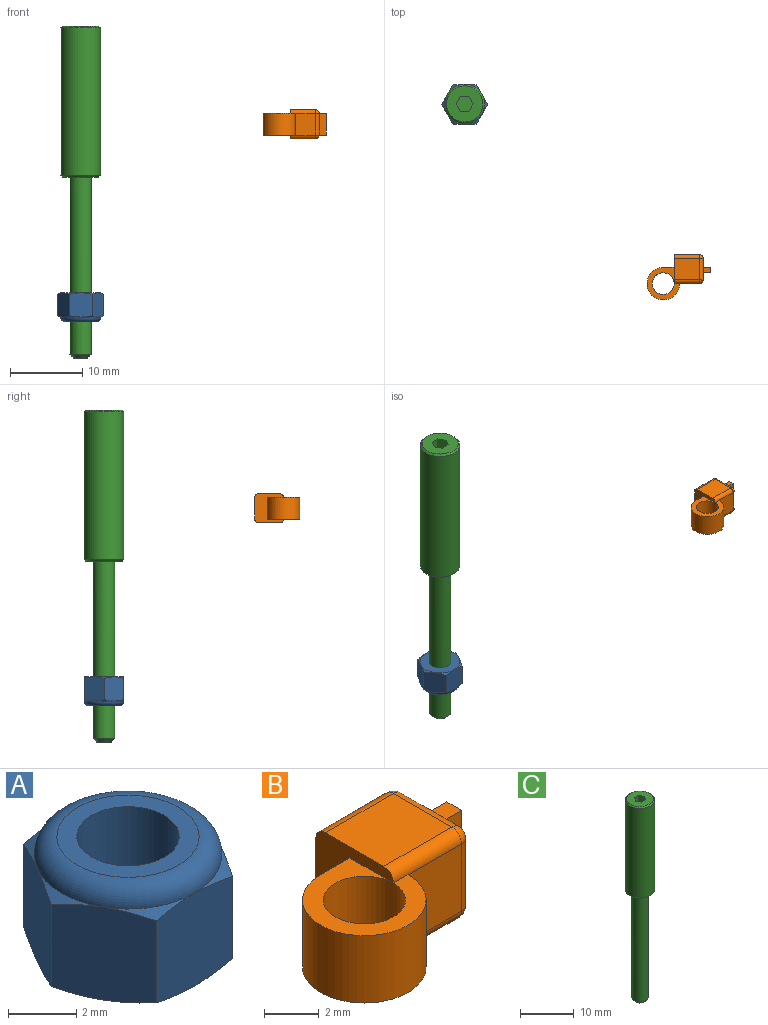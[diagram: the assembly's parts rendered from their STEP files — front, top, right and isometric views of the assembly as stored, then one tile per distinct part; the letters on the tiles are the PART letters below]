
ASSEMBLY  parts=3 mates=1
PART A: 22 faces, bbox 6.6x6.6x4.2 mm
  f0: plane 3.59x2.99mm, normal (-0.87,0.5,0), area 10.2mm2, adj f1,f5,f7,f9,f13,f14,f16,f21
  f1: plane 3.59x2.99mm, normal (-0.87,-0.5,0), area 10.2mm2, adj f0,f2,f7,f9,f10,f14,f20,f21
  f2: plane 3.6x3.42mm, normal (0,-1,0), area 10.2mm2, adj f1,f3,f7,f10,f11,f14,f19,f20
  f3: plane 3.59x2.99mm, normal (0.87,-0.5,0), area 10.2mm2, adj f2,f4,f7,f11,f12,f14,f18,f19
  f4: plane 3.59x2.99mm, normal (0.87,0.5,0), area 10.2mm2, adj f3,f5,f7,f12,f14,f15,f17,f18
  f5: plane 3.6x3.42mm, normal (0,1,0), area 10.2mm2, adj f0,f4,f7,f13,f14,f15,f16,f17
  f6: plane 4.17x4.17mm, normal (0,0,1), area 6.6mm2, adj f8,f14
  f7: plane 5.5x5.5mm, normal (0,0,-1), area 16.7mm2, adj f0,f1,f2,f3,f4,f5,f8,f16
  f8: cylinder r=1.5mm len=4mm, axis (0,0,1), area 37.7mm2, adj f6,f7
  f9: cone r=3.18mm half-angle=65deg, axis (0,0,-1), area 0.7mm2, adj f0,f1,f14
  f10: cone r=3.18mm half-angle=65deg, axis (0,0,-1), area 0.7mm2, adj f1,f2,f14
  f11: cone r=3.18mm half-angle=65deg, axis (0,0,-1), area 0.7mm2, adj f2,f3,f14
  f12: cone r=3.18mm half-angle=65deg, axis (0,0,-1), area 0.7mm2, adj f3,f4,f14
  f13: cone r=3.18mm half-angle=65deg, axis (0,0,-1), area 0.7mm2, adj f0,f5,f14
  f14: torus R=2.08mm, axis (0,0,-1), area 16.5mm2, adj f0,f1,f2,f3,f4,f5,f6,f9
  f15: cone r=3.18mm half-angle=65deg, axis (0,0,-1), area 0.7mm2, adj f4,f5,f14
  f16: cone r=2.75mm half-angle=65deg, axis (0,0,1), area 0.7mm2, adj f0,f5,f7
  f17: cone r=2.75mm half-angle=65deg, axis (0,0,1), area 0.7mm2, adj f4,f5,f7
  f18: cone r=2.75mm half-angle=65deg, axis (0,0,1), area 0.7mm2, adj f3,f4,f7
  f19: cone r=2.75mm half-angle=65deg, axis (0,0,1), area 0.7mm2, adj f2,f3,f7
  f20: cone r=2.75mm half-angle=65deg, axis (0,0,1), area 0.7mm2, adj f1,f2,f7
  f21: cone r=2.75mm half-angle=65deg, axis (0,0,1), area 0.7mm2, adj f0,f1,f7
PART B: 29 faces, bbox 8.8x6.3x4 mm
  f0: plane 3x1.25mm, normal (1,0,0), area 3.8mm2, adj f13,f18,f23,f24
  f1: cylinder r=2.25mm len=4.5mm, axis (0,0,-1), area 31.8mm2, adj f3,f4,f6,f16
  f2: cylinder r=1.5mm len=3mm, axis (0,0,-1), area 28.3mm2, adj f3,f4
  f3: plane 4.5x4.5mm, normal (0,0,1), area 8.2mm2, adj f1,f2,f5,f16,f22
  f4: plane 4.5x4.5mm, normal (0,0,-1), area 8.2mm2, adj f1,f2,f5,f16,f25
  f5: plane 4x4mm, normal (-1,0,0), area 9mm2, adj f3,f4,f8,f9,f10,f16,f17,f19
  f6: plane 3x2.75mm, normal (0,-1,0), area 8.2mm2, adj f1,f22,f25,f28
  f7: plane 3x1mm, normal (1,0,0), area 3mm2, adj f14,f23,f24,f28
  f8: plane 3.5x3mm, normal (0,1,0), area 10.5mm2, adj f5,f17,f18,f19
  f9: plane 3.5x3mm, normal (0,0,1), area 10.5mm2, adj f5,f17,f22,f23
  f10: plane 3.5x3mm, normal (0,0,-1), area 10.5mm2, adj f5,f19,f24,f25
  f11: plane 3x0.75mm, normal (1,0,0), area 2.2mm2, adj f12,f13,f14,f15
  f12: plane 1x0.75mm, normal (0,0,1), area 0.8mm2, adj f11,f13,f14,f23
  f13: plane 3x1mm, normal (0,1,0), area 3mm2, adj f0,f11,f12,f15
  f14: plane 3x1mm, normal (0,-1,0), area 3mm2, adj f7,f11,f12,f15
  f15: plane 1x0.75mm, normal (0,0,-1), area 0.8mm2, adj f11,f13,f14,f24
  f16: plane 3x1.5mm, normal (0,1,0), area 4.5mm2, adj f1,f3,f4,f5
  f17: cylinder r=0.5mm len=3.5mm, axis (1,0,0), area 2.7mm2, adj f5,f8,f9,f20
  f18: cylinder r=0.5mm len=3mm, axis (0,0,1), area 2.4mm2, adj f0,f8,f20,f21
  f19: cylinder r=0.5mm len=3.5mm, axis (-1,0,0), area 2.7mm2, adj f5,f8,f10,f21
  f20: sphere r=0.5mm, area 0.4mm2, adj f17,f18,f23
  f21: sphere r=0.5mm, area 0.4mm2, adj f18,f19,f24
  f22: cylinder r=0.5mm len=3.5mm, axis (-1,0,0), area 2.7mm2, adj f3,f5,f6,f9,f26
  f23: cylinder r=0.5mm len=3mm, axis (0,-1,0), area 2.4mm2, adj f0,f7,f9,f12,f20,f26
  f24: cylinder r=0.5mm len=3mm, axis (0,1,0), area 2.4mm2, adj f0,f7,f10,f15,f21,f27
  f25: cylinder r=0.5mm len=3.5mm, axis (1,0,0), area 2.7mm2, adj f4,f5,f6,f10,f27
  f26: sphere r=0.5mm, area 0.4mm2, adj f22,f23,f28
  f27: sphere r=0.5mm, area 0.4mm2, adj f24,f25,f28
  f28: cylinder r=0.5mm len=3mm, axis (0,0,-1), area 2.4mm2, adj f6,f7,f26,f27
PART C: 15 faces, bbox 5.5x5.5x45.9 mm
  f0: plane 5x5mm, normal (0,0,1), area 16.2mm2, adj f3,f4,f5,f6,f7,f8,f11
  f1: cylinder r=2.75mm len=20.4mm, axis (0,0,-1), area 352.5mm2, adj f10,f11
  f2: plane 5x5mm, normal (0,0,-1), area 12.6mm2, adj f10,f12
  f3: plane 1.5x1mm, normal (-0.87,-0.5,0), area 1.7mm2, adj f0,f4,f8,f9
  f4: plane 1.5x1.15mm, normal (0,-1,0), area 1.7mm2, adj f0,f3,f5,f9
  f5: plane 1.5x1mm, normal (0.87,-0.5,0), area 1.7mm2, adj f0,f4,f6,f9
  f6: plane 1.5x1mm, normal (0.87,0.5,0), area 1.7mm2, adj f0,f5,f7,f9
  f7: plane 1.5x1.15mm, normal (0,1,0), area 1.7mm2, adj f0,f6,f8,f9
  f8: plane 1.5x1mm, normal (-0.87,0.5,0), area 1.7mm2, adj f0,f3,f7,f9
  f9: plane 2.31x2mm, normal (0,0,1), area 3.5mm2, adj f3,f4,f5,f6,f7,f8
  f10: cone r=2.75mm half-angle=45deg, axis (0,0,1), area 5.8mm2, adj f1,f2
  f11: cone r=2.5mm half-angle=45deg, axis (0,0,-1), area 5.8mm2, adj f0,f1
  f12: cylinder r=1.5mm len=24.5mm, axis (0,0,1), area 230.9mm2, adj f2,f14
  f13: plane 2x2mm, normal (0,0,-1), area 3.1mm2, adj f14
  f14: cone r=1mm half-angle=45deg, axis (0,0,1), area 5.6mm2, adj f12,f13
PLACE A rot(axis=(1,0,0),180deg) t=(-50,0,-16)mm
PLACE B t=(-22.55,-24.82,5.81)mm
PLACE C at identity fixed
MATE fastened A.f8 <-> C.f1  axis (0,0,-1) through (-50,0,-16)mm
